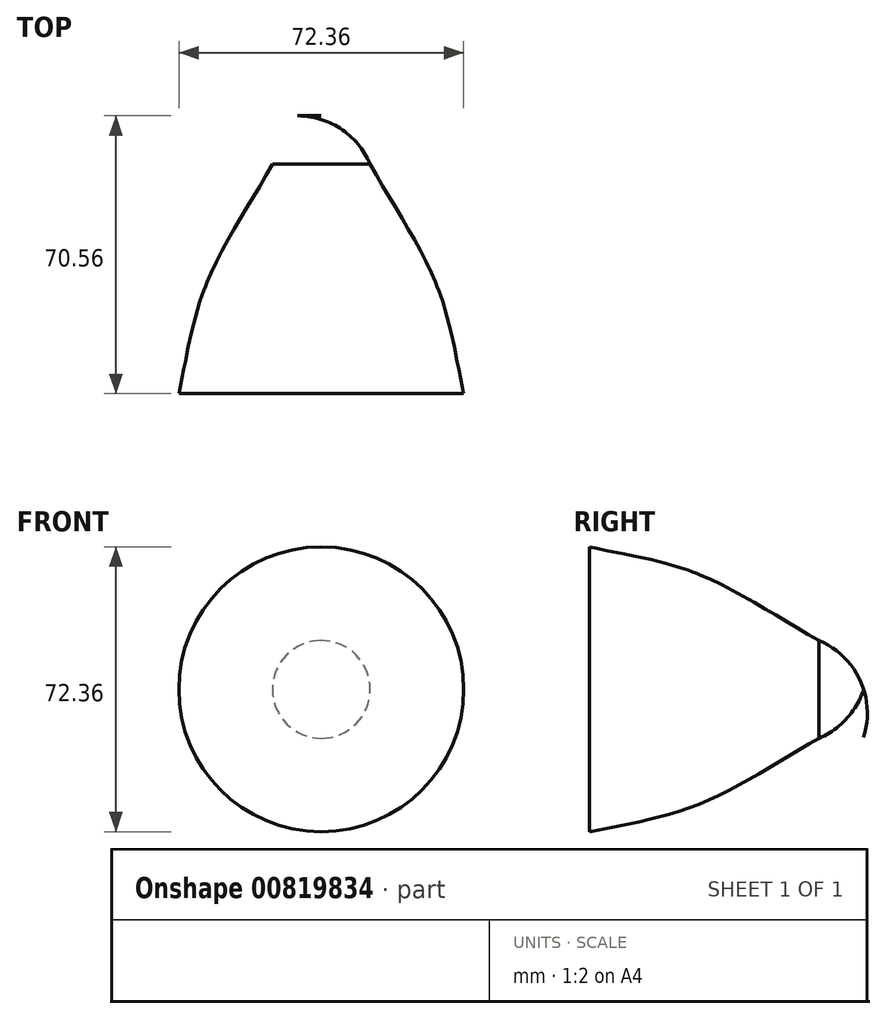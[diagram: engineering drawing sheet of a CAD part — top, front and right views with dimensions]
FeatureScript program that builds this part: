
annotation { "Feature Type Name" : "Feature", "Feature Type Description" : "" }
export const myFeature = defineFeature(function(context is Context, id is Id, definition is map)
    precondition{}
    {
        {
            var Q0;
            Q0=qCreatedBy(makeId("Right.planeOp"),FACE);
            var sketch = newSketch(context, id + "F0", { "sketchPlane" : qUnion([Q0])});
            skFitSpline(sketch, "E0", {"points": [v(58.25, 12.41) * mm, v(27.45, 29.34) * mm, v(0, 36.18) * mm], "startDerivative": vector(-58.5, 32.75) * mm, "endDerivative": vector(-57.99, 12.67) * mm});
            skArc(sketch, "E1", {"start": v(69.62, 0) * mm, "mid": v(65.3, 7.46) * mm, "end": v(58.25, 12.41) * mm});
            skLineSegment(sketch, "E2", {"start": v(0, 36.18) * mm, "end": v(0, 0) * mm});
            skLineSegment(sketch, "E3", {"start": v(0, 0) * mm, "end": v(69.62, 0) * mm});
            skSolve(sketch);
        }
        {
            var Q0;
            Q0 = qSketchRegion(id + "F0", true);
            var Q1;
            Q1=sQuery(id+"F0.wireOp",EDGE,"E3");
            revolve(context, id + "F1", {"surfaceOperationType" : NewSurfaceOperationType.NEW, "entities" : qUnion([Q0]), "axis" : qUnion([Q1]), "revolveType" : RevolveType.FULL});
        }
        {
            var Q0;
            Q0=qCreatedBy(makeId("Right.planeOp"),FACE);
            var sketch = newSketch(context, id + "F2", { "sketchPlane" : qUnion([Q0])});
            skFitSpline(sketch, "E4", {"points": [v(24.88, 209.27) * mm, v(46.57, 76.1) * mm, v(52.4, 0) * mm], "startDerivative": vector(44.97, -249.32) * mm, "endDerivative": vector(8.33, -165.25) * mm});
            skLineSegment(sketch, "E5", {"start": v(0, 209.27) * mm, "end": v(24.88, 0) * mm});
            skSolve(sketch);
        }
        {
            var Q0;
            Q0 = qSketchRegion(id + "F2", true);
            var Q1;
            Q1=sQuery(id+"F2.wireOp",EDGE,"E4");
            var Q2;
            Q2=sQuery(id+"F2.wireOp",EDGE,"E5");
            revolve(context, id + "F3", {"bodyType" : ToolBodyType.SURFACE, "surfaceOperationType" : NewSurfaceOperationType.NEW, "entities" : qUnion([Q0]), "surfaceEntities" : qUnion([Q1]), "axis" : qUnion([Q2]), "revolveType" : RevolveType.SYMMETRIC, "angle" : 58.95 * degree});
        }
        {
            var Q0;
            Q0=makeQuery(id+"F3.opRevolve","SWEPT_BODY",BODY,{"disambiguationData":[OSD([sQuery(id+"F2.wireOp",EDGE,"E4")])]});
            var Q1;
            Q1=makeQuery(id+"F1.opRevolve","SWEPT_EDGE",EDGE,{"disambiguationData":[OSD([sQuery(id+"F0.wireOp",EDGE,"E0"),sQuery(id+"F0.wireOp",EDGE,"E1")])]});
            circularPattern(context, id + "F4", {"entities" : qUnion([Q0]), "axis" : qUnion([Q1]), "angle" : 360 * degree, "instanceCount" : 3, "equalSpace" : true});
        }
    });
